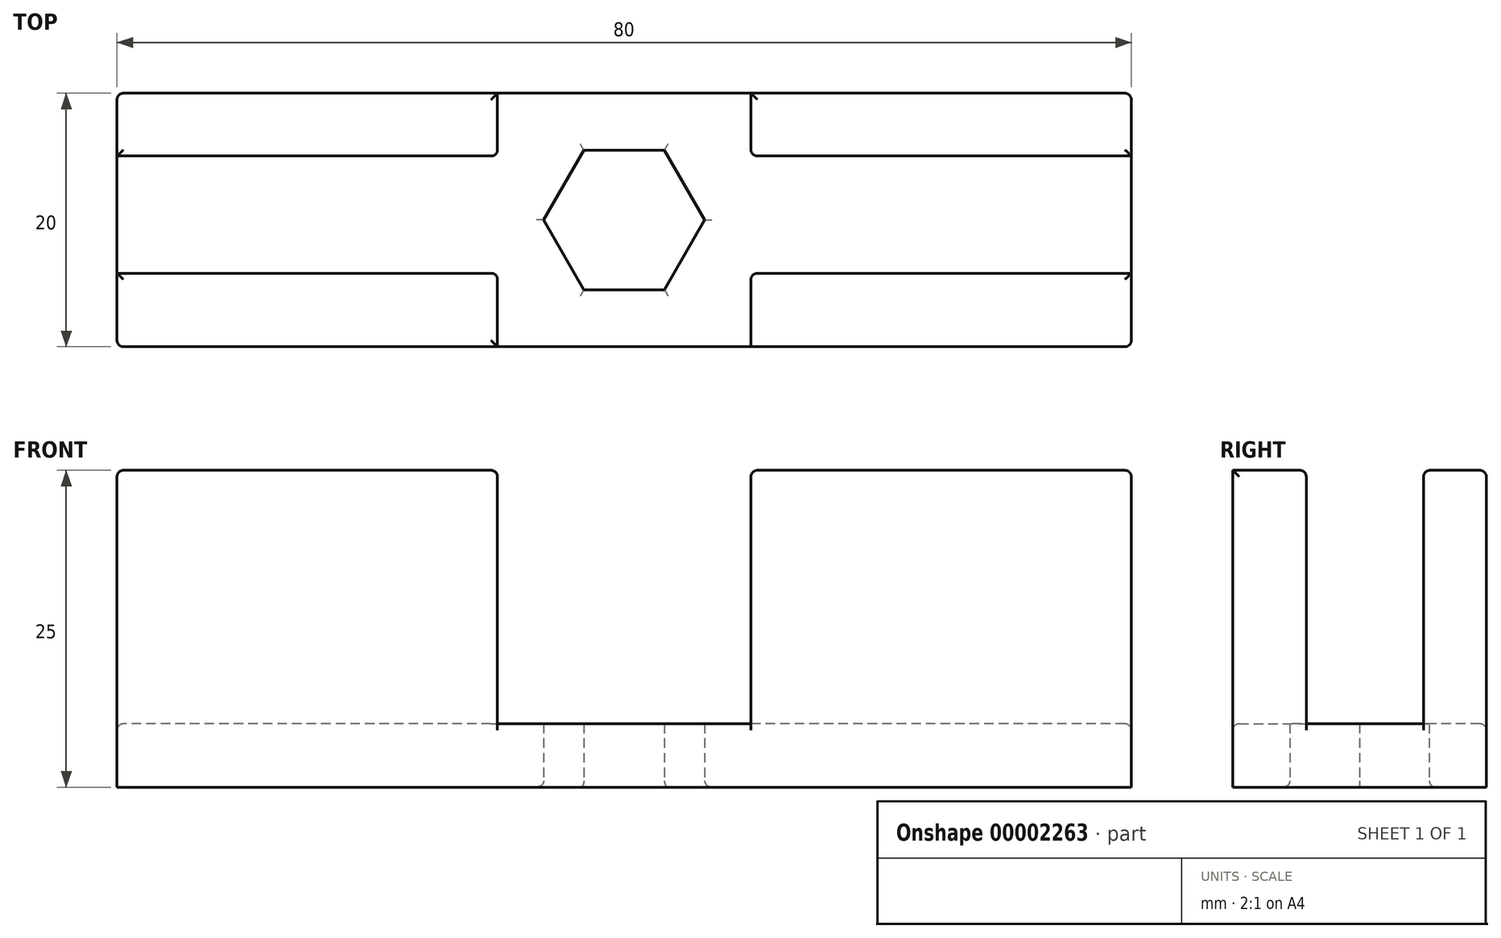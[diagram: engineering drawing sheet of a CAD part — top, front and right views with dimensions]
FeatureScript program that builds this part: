
annotation { "Feature Type Name" : "Feature", "Feature Type Description" : "" }
export const myFeature = defineFeature(function(context is Context, id is Id, definition is map)
    precondition{}
    {
        {
            var Q0;
            Q0=qCreatedBy(makeId("Top.planeOp"),FACE);
            var sketch = newSketch(context, id + "F0", { "sketchPlane" : qUnion([Q0])});
            skCircle(sketch, "E0.cCircle", {"center": v(0, 0) * mm, "radius": 5.5 * mm, "construction": true});
            skLineSegment(sketch, "E0.0", {"start": v(6.35, 0) * mm, "end": v(3.18, -5.5) * mm});
            skLineSegment(sketch, "E0.1", {"start": v(3.18, -5.5) * mm, "end": v(-3.18, -5.5) * mm});
            skLineSegment(sketch, "E0.2", {"start": v(-3.18, -5.5) * mm, "end": v(-6.35, 0) * mm});
            skLineSegment(sketch, "E0.3", {"start": v(-6.35, 0) * mm, "end": v(-3.18, 5.5) * mm});
            skLineSegment(sketch, "E0.4", {"start": v(-3.18, 5.5) * mm, "end": v(3.18, 5.5) * mm});
            skLineSegment(sketch, "E0.5", {"start": v(3.18, 5.5) * mm, "end": v(6.35, 0) * mm});
            skPoint(sketch, "E0.0.midPoint", {"position": v(4.76, -2.75) * mm});
            skLineSegment(sketch, "E1.bottom", {"start": v(40, -10) * mm, "end": v(-40, -10) * mm});
            skLineSegment(sketch, "E1.top", {"start": v(40, 10) * mm, "end": v(-40, 10) * mm});
            skLineSegment(sketch, "E1.left", {"start": v(40, -10) * mm, "end": v(40, 10) * mm});
            skLineSegment(sketch, "E1.right", {"start": v(-40, -10) * mm, "end": v(-40, 10) * mm});
            skSolve(sketch);
        }
        {
            var Q0;
            Q0=makeQuery(id+"F0.imprint","IMPRINT",FACE,{"disambiguationData":[TD([[makeQuery(id+"F0.imprint","IMPRINT",EDGE,{"derivedFrom":sQuery(id+"F0.wireOp",EDGE,"E0.0")}),1.0]])]});
            extrude(context, id + "F1", {"entities" : qUnion([Q0]), "depth" : 5 * mm});
        }
        {
            var Q0;
            Q0=makeQuery(id+"F1.opExtrude","CAP_FACE",FACE,{"disambiguationData":[OSD([sQuery(id+"F0.wireOp",EDGE,"E0.0"),sQuery(id+"F0.wireOp",EDGE,"E0.1"),sQuery(id+"F0.wireOp",EDGE,"E0.2"),sQuery(id+"F0.wireOp",EDGE,"E0.3"),sQuery(id+"F0.wireOp",EDGE,"E0.4"),sQuery(id+"F0.wireOp",EDGE,"E0.5"),sQuery(id+"F0.wireOp",EDGE,"E1.bottom"),sQuery(id+"F0.wireOp",EDGE,"E1.top"),sQuery(id+"F0.wireOp",EDGE,"E1.left"),sQuery(id+"F0.wireOp",EDGE,"E1.right")])],"isStart":false});
            var sketch = newSketch(context, id + "F2", { "sketchPlane" : qUnion([Q0])});
            skLineSegment(sketch, "E2", {"start": v(40, -4.2) * mm, "end": v(-40, -4.2) * mm});
            skLineSegment(sketch, "E3", {"start": v(40, 5.05) * mm, "end": v(-40, 5.05) * mm});
            skLineSegment(sketch, "E4", {"start": v(10, 10) * mm, "end": v(10, -10) * mm});
            skLineSegment(sketch, "E5", {"start": v(-10, -10) * mm, "end": v(-10, 10) * mm});
            skSolve(sketch);
        }
        {
            var Q0;
            {var subQ0=sQuery(id+"F2.wireOp",EDGE,"E3");var subQ1=makeQuery(id+"F1.opExtrude","CAP_EDGE",EDGE,{"disambiguationData":[OSD([sQuery(id+"F0.wireOp",EDGE,"E1.left")])],"isStart":false});var subQ2=makeQuery(id+"F2.imprint","INTERSECT",VERTEX,{"derivedFrom":[subQ1,subQ0]});Q0=makeQuery(id+"F2.imprint","IMPRINT",FACE,{"disambiguationData":[TD([[makeQuery(id+"F2.imprint","IMPRINT",EDGE,{"disambiguationData":[TD([[subQ2,-1.0]])],"derivedFrom":subQ0}),-1.0]])]});}
            var Q1;
            {var subQ0=sQuery(id+"F2.wireOp",EDGE,"E2");var subQ1=makeQuery(id+"F1.opExtrude","CAP_EDGE",EDGE,{"disambiguationData":[OSD([sQuery(id+"F0.wireOp",EDGE,"E1.left")])],"isStart":false});var subQ2=makeQuery(id+"F2.imprint","INTERSECT",VERTEX,{"derivedFrom":[subQ1,subQ0]});Q1=makeQuery(id+"F2.imprint","IMPRINT",FACE,{"disambiguationData":[TD([[makeQuery(id+"F2.imprint","IMPRINT",EDGE,{"disambiguationData":[TD([[subQ2,-1.0]])],"derivedFrom":subQ0}),1.0]])]});}
            var Q2;
            {var subQ0=sQuery(id+"F2.wireOp",EDGE,"E2");var subQ1=makeQuery(id+"F1.opExtrude","CAP_EDGE",EDGE,{"disambiguationData":[OSD([sQuery(id+"F0.wireOp",EDGE,"E1.right")])],"isStart":false});var subQ2=makeQuery(id+"F2.imprint","INTERSECT",VERTEX,{"derivedFrom":[subQ1,subQ0]});Q2=makeQuery(id+"F2.imprint","IMPRINT",FACE,{"disambiguationData":[TD([[makeQuery(id+"F2.imprint","IMPRINT",EDGE,{"disambiguationData":[TD([[subQ2,1.0]])],"derivedFrom":subQ0}),1.0]])]});}
            var Q3;
            {var subQ0=sQuery(id+"F2.wireOp",EDGE,"E3");var subQ1=makeQuery(id+"F1.opExtrude","CAP_EDGE",EDGE,{"disambiguationData":[OSD([sQuery(id+"F0.wireOp",EDGE,"E1.right")])],"isStart":false});var subQ2=makeQuery(id+"F2.imprint","INTERSECT",VERTEX,{"derivedFrom":[subQ1,subQ0]});Q3=makeQuery(id+"F2.imprint","IMPRINT",FACE,{"disambiguationData":[TD([[makeQuery(id+"F2.imprint","IMPRINT",EDGE,{"disambiguationData":[TD([[subQ2,1.0]])],"derivedFrom":subQ0}),-1.0]])]});}
            extrude(context, id + "F3", {"entities" : qUnion([Q0, Q1, Q2, Q3]), "operationType" : NewBodyOperationType.ADD, "depth" : 20 * mm});
        }
        {
            var Q0;
            Q0=makeQuery(id+"F1.opExtrude","CAP_EDGE",EDGE,{"disambiguationData":[OSD([sQuery(id+"F0.wireOp",EDGE,"E0.0")])],"isStart":true});
            var Q1;
            Q1=makeQuery(id+"F1.opExtrude","CAP_EDGE",EDGE,{"disambiguationData":[OSD([sQuery(id+"F0.wireOp",EDGE,"E0.5")])],"isStart":true});
            var Q2;
            Q2=makeQuery(id+"F1.opExtrude","CAP_EDGE",EDGE,{"disambiguationData":[OSD([sQuery(id+"F0.wireOp",EDGE,"E0.1")])],"isStart":true});
            var Q3;
            Q3=makeQuery(id+"F1.opExtrude","CAP_EDGE",EDGE,{"disambiguationData":[OSD([sQuery(id+"F0.wireOp",EDGE,"E0.2")])],"isStart":true});
            var Q4;
            Q4=makeQuery(id+"F1.opExtrude","CAP_EDGE",EDGE,{"disambiguationData":[OSD([sQuery(id+"F0.wireOp",EDGE,"E0.3")])],"isStart":true});
            var Q5;
            Q5=makeQuery(id+"F1.opExtrude","CAP_EDGE",EDGE,{"disambiguationData":[OSD([sQuery(id+"F0.wireOp",EDGE,"E0.4")])],"isStart":true});
            var Q6;
            {var subQ0=sQuery(id+"F2.wireOp",EDGE,"E2");Q6=makeQuery(id+"F3.opExtrude","CAP_EDGE",EDGE,{"disambiguationData":[OSD([subQ0]),TDD([makeQuery(id+"F2.imprint","IMPRINT",EDGE,{"disambiguationData":[TD([[makeQuery(id+"F2.imprint","INTERSECT",VERTEX,{"derivedFrom":[makeQuery(id+"F1.opExtrude","CAP_EDGE",EDGE,{"disambiguationData":[OSD([sQuery(id+"F0.wireOp",EDGE,"E1.right")])],"isStart":false}),subQ0]}),1.0]])],"derivedFrom":subQ0})])],"isStart":true});}
            var Q7;
            {var subQ0=sQuery(id+"F2.wireOp",EDGE,"E2");Q7=makeQuery(id+"F3.opExtrude","CAP_EDGE",EDGE,{"disambiguationData":[OSD([subQ0]),TDD([makeQuery(id+"F2.imprint","IMPRINT",EDGE,{"disambiguationData":[TD([[makeQuery(id+"F2.imprint","INTERSECT",VERTEX,{"derivedFrom":[makeQuery(id+"F1.opExtrude","CAP_EDGE",EDGE,{"disambiguationData":[OSD([sQuery(id+"F0.wireOp",EDGE,"E1.left")])],"isStart":false}),subQ0]}),-1.0]])],"derivedFrom":subQ0})])],"isStart":true});}
            var Q8;
            {var subQ0=sQuery(id+"F2.wireOp",EDGE,"E3");Q8=makeQuery(id+"F3.opExtrude","CAP_EDGE",EDGE,{"disambiguationData":[OSD([subQ0]),TDD([makeQuery(id+"F2.imprint","IMPRINT",EDGE,{"disambiguationData":[TD([[makeQuery(id+"F2.imprint","INTERSECT",VERTEX,{"derivedFrom":[makeQuery(id+"F1.opExtrude","CAP_EDGE",EDGE,{"disambiguationData":[OSD([sQuery(id+"F0.wireOp",EDGE,"E1.left")])],"isStart":false}),subQ0]}),-1.0]])],"derivedFrom":subQ0})])],"isStart":true});}
            var Q9;
            {var subQ0=sQuery(id+"F2.wireOp",EDGE,"E3");Q9=makeQuery(id+"F3.opExtrude","CAP_EDGE",EDGE,{"disambiguationData":[OSD([subQ0]),TDD([makeQuery(id+"F2.imprint","IMPRINT",EDGE,{"disambiguationData":[TD([[makeQuery(id+"F2.imprint","INTERSECT",VERTEX,{"derivedFrom":[makeQuery(id+"F1.opExtrude","CAP_EDGE",EDGE,{"disambiguationData":[OSD([sQuery(id+"F0.wireOp",EDGE,"E1.right")])],"isStart":false}),subQ0]}),1.0]])],"derivedFrom":subQ0})])],"isStart":true});}
            var Q10;
            Q10=makeQuery(id+"F3.opExtrude","SWEPT_EDGE",EDGE,{"disambiguationData":[OSD([sQuery(id+"F2.wireOp",EDGE,"E2"),sQuery(id+"F2.wireOp",EDGE,"E4")])]});
            var Q11;
            Q11=makeQuery(id+"F3.opExtrude","SWEPT_EDGE",EDGE,{"disambiguationData":[OSD([sQuery(id+"F2.wireOp",EDGE,"E2"),sQuery(id+"F2.wireOp",EDGE,"E5")])]});
            var Q12;
            Q12=makeQuery(id+"F3.opExtrude","SWEPT_EDGE",EDGE,{"disambiguationData":[OSD([sQuery(id+"F2.wireOp",EDGE,"E3"),sQuery(id+"F2.wireOp",EDGE,"E4")])]});
            var Q13;
            Q13=makeQuery(id+"F3.opExtrude","SWEPT_EDGE",EDGE,{"disambiguationData":[OSD([sQuery(id+"F2.wireOp",EDGE,"E3"),sQuery(id+"F2.wireOp",EDGE,"E5")])]});
            var Q14;
            {var subQ0=sQuery(id+"F2.wireOp",EDGE,"E3");Q14=makeQuery(id+"F3.opExtrude","CAP_EDGE",EDGE,{"disambiguationData":[OSD([subQ0]),TDD([makeQuery(id+"F2.imprint","IMPRINT",EDGE,{"disambiguationData":[TD([[makeQuery(id+"F2.imprint","INTERSECT",VERTEX,{"derivedFrom":[makeQuery(id+"F1.opExtrude","CAP_EDGE",EDGE,{"disambiguationData":[OSD([sQuery(id+"F0.wireOp",EDGE,"E1.right")])],"isStart":false}),subQ0]}),1.0]])],"derivedFrom":subQ0})])],"isStart":false});}
            var Q15;
            {var subQ0=sQuery(id+"F2.wireOp",EDGE,"E2");Q15=makeQuery(id+"F3.opExtrude","CAP_EDGE",EDGE,{"disambiguationData":[OSD([subQ0]),TDD([makeQuery(id+"F2.imprint","IMPRINT",EDGE,{"disambiguationData":[TD([[makeQuery(id+"F2.imprint","INTERSECT",VERTEX,{"derivedFrom":[makeQuery(id+"F1.opExtrude","CAP_EDGE",EDGE,{"disambiguationData":[OSD([sQuery(id+"F0.wireOp",EDGE,"E1.right")])],"isStart":false}),subQ0]}),1.0]])],"derivedFrom":subQ0})])],"isStart":false});}
            var Q16;
            {var subQ0=sQuery(id+"F2.wireOp",EDGE,"E2");Q16=makeQuery(id+"F3.opExtrude","CAP_EDGE",EDGE,{"disambiguationData":[OSD([subQ0]),TDD([makeQuery(id+"F2.imprint","IMPRINT",EDGE,{"disambiguationData":[TD([[makeQuery(id+"F2.imprint","INTERSECT",VERTEX,{"derivedFrom":[makeQuery(id+"F1.opExtrude","CAP_EDGE",EDGE,{"disambiguationData":[OSD([sQuery(id+"F0.wireOp",EDGE,"E1.left")])],"isStart":false}),subQ0]}),-1.0]])],"derivedFrom":subQ0})])],"isStart":false});}
            var Q17;
            {var subQ0=sQuery(id+"F2.wireOp",EDGE,"E3");Q17=makeQuery(id+"F3.opExtrude","CAP_EDGE",EDGE,{"disambiguationData":[OSD([subQ0]),TDD([makeQuery(id+"F2.imprint","IMPRINT",EDGE,{"disambiguationData":[TD([[makeQuery(id+"F2.imprint","INTERSECT",VERTEX,{"derivedFrom":[makeQuery(id+"F1.opExtrude","CAP_EDGE",EDGE,{"disambiguationData":[OSD([sQuery(id+"F0.wireOp",EDGE,"E1.left")])],"isStart":false}),subQ0]}),-1.0]])],"derivedFrom":subQ0})])],"isStart":false});}
            var Q18;
            {var subQ0=sQuery(id+"F2.wireOp",EDGE,"E4");Q18=makeQuery(id+"F3.opExtrude","CAP_EDGE",EDGE,{"disambiguationData":[OSD([subQ0]),TDD([makeQuery(id+"F2.imprint","IMPRINT",EDGE,{"disambiguationData":[TD([[makeQuery(id+"F2.imprint","INTERSECT",VERTEX,{"derivedFrom":[makeQuery(id+"F1.opExtrude","CAP_EDGE",EDGE,{"disambiguationData":[OSD([sQuery(id+"F0.wireOp",EDGE,"E1.bottom")])],"isStart":false}),subQ0]}),1.0]])],"derivedFrom":subQ0})])],"isStart":false});}
            var Q19;
            {var subQ0=sQuery(id+"F2.wireOp",EDGE,"E5");Q19=makeQuery(id+"F3.opExtrude","CAP_EDGE",EDGE,{"disambiguationData":[OSD([subQ0]),TDD([makeQuery(id+"F2.imprint","IMPRINT",EDGE,{"disambiguationData":[TD([[makeQuery(id+"F2.imprint","INTERSECT",VERTEX,{"derivedFrom":[makeQuery(id+"F1.opExtrude","CAP_EDGE",EDGE,{"disambiguationData":[OSD([sQuery(id+"F0.wireOp",EDGE,"E1.bottom")])],"isStart":false}),subQ0]}),-1.0]])],"derivedFrom":subQ0})])],"isStart":false});}
            var Q20;
            {var subQ0=sQuery(id+"F2.wireOp",EDGE,"E4");Q20=makeQuery(id+"F3.opExtrude","CAP_EDGE",EDGE,{"disambiguationData":[OSD([subQ0]),TDD([makeQuery(id+"F2.imprint","IMPRINT",EDGE,{"disambiguationData":[TD([[makeQuery(id+"F2.imprint","INTERSECT",VERTEX,{"derivedFrom":[makeQuery(id+"F1.opExtrude","CAP_EDGE",EDGE,{"disambiguationData":[OSD([sQuery(id+"F0.wireOp",EDGE,"E1.top")])],"isStart":false}),subQ0]}),-1.0]])],"derivedFrom":subQ0})])],"isStart":false});}
            var Q21;
            {var subQ0=sQuery(id+"F2.wireOp",EDGE,"E5");Q21=makeQuery(id+"F3.opExtrude","CAP_EDGE",EDGE,{"disambiguationData":[OSD([subQ0]),TDD([makeQuery(id+"F2.imprint","IMPRINT",EDGE,{"disambiguationData":[TD([[makeQuery(id+"F2.imprint","INTERSECT",VERTEX,{"derivedFrom":[makeQuery(id+"F1.opExtrude","CAP_EDGE",EDGE,{"disambiguationData":[OSD([sQuery(id+"F0.wireOp",EDGE,"E1.top")])],"isStart":false}),subQ0]}),1.0]])],"derivedFrom":subQ0})])],"isStart":false});}
            var Q22;
            Q22=makeQuery(id+"F1.opExtrude","CAP_EDGE",EDGE,{"disambiguationData":[OSD([sQuery(id+"F0.wireOp",EDGE,"E1.right")])],"isStart":false});
            var Q23;
            Q23=makeQuery(id+"F1.opExtrude","CAP_EDGE",EDGE,{"disambiguationData":[OSD([sQuery(id+"F0.wireOp",EDGE,"E1.bottom")])],"isStart":false});
            var Q24;
            Q24=makeQuery(id+"F1.opExtrude","CAP_EDGE",EDGE,{"disambiguationData":[OSD([sQuery(id+"F0.wireOp",EDGE,"E1.left")])],"isStart":false});
            var Q25;
            Q25=makeQuery(id+"F1.opExtrude","CAP_EDGE",EDGE,{"disambiguationData":[OSD([sQuery(id+"F0.wireOp",EDGE,"E1.top")])],"isStart":false});
            var Q26;
            {var subQ0=sQuery(id+"F0.wireOp",EDGE,"E1.right");var subQ1=sQuery(id+"F0.wireOp",EDGE,"E1.bottom");Q26=makeQuery(id+"F3.boolean.opBoolean","MERGE",EDGE,{"derivedFrom":[makeQuery(id+"F1.opExtrude","SWEPT_EDGE",EDGE,{"disambiguationData":[OSD([subQ1,subQ0])]}),makeQuery(id+"F3.opExtrude","SWEPT_EDGE",EDGE,{"disambiguationData":[OSD([subQ1,subQ0])]})]});}
            var Q27;
            {var subQ0=sQuery(id+"F0.wireOp",EDGE,"E1.right");var subQ1=sQuery(id+"F0.wireOp",EDGE,"E1.top");Q27=makeQuery(id+"F3.boolean.opBoolean","MERGE",EDGE,{"derivedFrom":[makeQuery(id+"F1.opExtrude","SWEPT_EDGE",EDGE,{"disambiguationData":[OSD([subQ1,subQ0])]}),makeQuery(id+"F3.opExtrude","SWEPT_EDGE",EDGE,{"disambiguationData":[OSD([subQ1,subQ0])]})]});}
            var Q28;
            {var subQ0=sQuery(id+"F0.wireOp",EDGE,"E1.left");var subQ1=sQuery(id+"F0.wireOp",EDGE,"E1.bottom");Q28=makeQuery(id+"F3.boolean.opBoolean","MERGE",EDGE,{"derivedFrom":[makeQuery(id+"F1.opExtrude","SWEPT_EDGE",EDGE,{"disambiguationData":[OSD([subQ1,subQ0])]}),makeQuery(id+"F3.opExtrude","SWEPT_EDGE",EDGE,{"disambiguationData":[OSD([subQ1,subQ0])]})]});}
            var Q29;
            {var subQ0=sQuery(id+"F0.wireOp",EDGE,"E1.left");var subQ1=sQuery(id+"F0.wireOp",EDGE,"E1.top");Q29=makeQuery(id+"F3.boolean.opBoolean","MERGE",EDGE,{"derivedFrom":[makeQuery(id+"F1.opExtrude","SWEPT_EDGE",EDGE,{"disambiguationData":[OSD([subQ1,subQ0])]}),makeQuery(id+"F3.opExtrude","SWEPT_EDGE",EDGE,{"disambiguationData":[OSD([subQ1,subQ0])]})]});}
            var Q30;
            {var subQ0=sQuery(id+"F0.wireOp",EDGE,"E1.top");var subQ1=makeQuery(id+"F1.opExtrude","CAP_EDGE",EDGE,{"disambiguationData":[OSD([subQ0])],"isStart":false});Q30=makeQuery(id+"F3.opExtrude","CAP_EDGE",EDGE,{"disambiguationData":[OSD([subQ0]),TDD([makeQuery(id+"F2.imprint","IMPRINT",EDGE,{"disambiguationData":[TD([[makeQuery(id+"F2.imprint","INTERSECT",VERTEX,{"derivedFrom":[subQ1,makeQuery(id+"F1.opExtrude","CAP_EDGE",EDGE,{"disambiguationData":[OSD([sQuery(id+"F0.wireOp",EDGE,"E1.right")])],"isStart":false})]}),1.0]])],"derivedFrom":subQ1})])],"isStart":false});}
            var Q31;
            {var subQ0=sQuery(id+"F0.wireOp",EDGE,"E1.right");var subQ1=makeQuery(id+"F1.opExtrude","CAP_EDGE",EDGE,{"disambiguationData":[OSD([subQ0])],"isStart":false});Q31=makeQuery(id+"F3.opExtrude","CAP_EDGE",EDGE,{"disambiguationData":[OSD([subQ0]),TDD([makeQuery(id+"F2.imprint","IMPRINT",EDGE,{"disambiguationData":[TD([[makeQuery(id+"F2.imprint","INTERSECT",VERTEX,{"derivedFrom":[makeQuery(id+"F1.opExtrude","CAP_EDGE",EDGE,{"disambiguationData":[OSD([sQuery(id+"F0.wireOp",EDGE,"E1.top")])],"isStart":false}),subQ1]}),1.0]])],"derivedFrom":subQ1})])],"isStart":false});}
            var Q32;
            {var subQ0=sQuery(id+"F0.wireOp",EDGE,"E1.top");var subQ1=makeQuery(id+"F1.opExtrude","CAP_EDGE",EDGE,{"disambiguationData":[OSD([subQ0])],"isStart":false});Q32=makeQuery(id+"F3.opExtrude","CAP_EDGE",EDGE,{"disambiguationData":[OSD([subQ0]),TDD([makeQuery(id+"F2.imprint","IMPRINT",EDGE,{"disambiguationData":[TD([[makeQuery(id+"F2.imprint","INTERSECT",VERTEX,{"derivedFrom":[subQ1,makeQuery(id+"F1.opExtrude","CAP_EDGE",EDGE,{"disambiguationData":[OSD([sQuery(id+"F0.wireOp",EDGE,"E1.left")])],"isStart":false})]}),-1.0]])],"derivedFrom":subQ1})])],"isStart":false});}
            var Q33;
            {var subQ0=sQuery(id+"F0.wireOp",EDGE,"E1.left");var subQ1=makeQuery(id+"F1.opExtrude","CAP_EDGE",EDGE,{"disambiguationData":[OSD([subQ0])],"isStart":false});Q33=makeQuery(id+"F3.opExtrude","CAP_EDGE",EDGE,{"disambiguationData":[OSD([subQ0]),TDD([makeQuery(id+"F2.imprint","IMPRINT",EDGE,{"disambiguationData":[TD([[makeQuery(id+"F2.imprint","INTERSECT",VERTEX,{"derivedFrom":[makeQuery(id+"F1.opExtrude","CAP_EDGE",EDGE,{"disambiguationData":[OSD([sQuery(id+"F0.wireOp",EDGE,"E1.top")])],"isStart":false}),subQ1]}),1.0]])],"derivedFrom":subQ1})])],"isStart":false});}
            var Q34;
            {var subQ0=sQuery(id+"F0.wireOp",EDGE,"E1.left");var subQ1=makeQuery(id+"F1.opExtrude","CAP_EDGE",EDGE,{"disambiguationData":[OSD([subQ0])],"isStart":false});Q34=makeQuery(id+"F3.opExtrude","CAP_EDGE",EDGE,{"disambiguationData":[OSD([subQ0]),TDD([makeQuery(id+"F2.imprint","IMPRINT",EDGE,{"disambiguationData":[TD([[makeQuery(id+"F2.imprint","INTERSECT",VERTEX,{"derivedFrom":[makeQuery(id+"F1.opExtrude","CAP_EDGE",EDGE,{"disambiguationData":[OSD([sQuery(id+"F0.wireOp",EDGE,"E1.bottom")])],"isStart":false}),subQ1]}),-1.0]])],"derivedFrom":subQ1})])],"isStart":false});}
            var Q35;
            {var subQ0=sQuery(id+"F0.wireOp",EDGE,"E1.bottom");var subQ1=makeQuery(id+"F1.opExtrude","CAP_EDGE",EDGE,{"disambiguationData":[OSD([subQ0])],"isStart":false});Q35=makeQuery(id+"F3.opExtrude","CAP_EDGE",EDGE,{"disambiguationData":[OSD([subQ0]),TDD([makeQuery(id+"F2.imprint","IMPRINT",EDGE,{"disambiguationData":[TD([[makeQuery(id+"F2.imprint","INTERSECT",VERTEX,{"derivedFrom":[subQ1,makeQuery(id+"F1.opExtrude","CAP_EDGE",EDGE,{"disambiguationData":[OSD([sQuery(id+"F0.wireOp",EDGE,"E1.right")])],"isStart":false})]}),1.0]])],"derivedFrom":subQ1})])],"isStart":false});}
            var Q36;
            {var subQ0=sQuery(id+"F0.wireOp",EDGE,"E1.right");var subQ1=makeQuery(id+"F1.opExtrude","CAP_EDGE",EDGE,{"disambiguationData":[OSD([subQ0])],"isStart":false});Q36=makeQuery(id+"F3.opExtrude","CAP_EDGE",EDGE,{"disambiguationData":[OSD([subQ0]),TDD([makeQuery(id+"F2.imprint","IMPRINT",EDGE,{"disambiguationData":[TD([[makeQuery(id+"F2.imprint","INTERSECT",VERTEX,{"derivedFrom":[makeQuery(id+"F1.opExtrude","CAP_EDGE",EDGE,{"disambiguationData":[OSD([sQuery(id+"F0.wireOp",EDGE,"E1.bottom")])],"isStart":false}),subQ1]}),-1.0]])],"derivedFrom":subQ1})])],"isStart":false});}
            fillet(context, id + "F4", {"entities" : qUnion([Q0, Q1, Q2, Q3, Q4, Q5, Q6, Q7, Q8, Q9, Q10, Q11, Q12, Q13, Q14, Q15, Q16, Q17, Q18, Q19, Q20, Q21, Q22, Q23, Q24, Q25, Q26, Q27, Q28, Q29, Q30, Q31, Q32, Q33, Q34, Q35, Q36]), "radius" : .5 * mm, "tangentPropagation" : true, "allowEdgeOverflow" : false});
        }
    });
